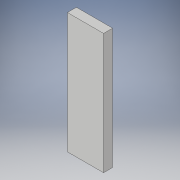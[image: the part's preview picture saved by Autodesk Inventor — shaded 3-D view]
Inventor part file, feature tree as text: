
AUTODESK INVENTOR PART (.ipt)
format: ipt  version: 2017 (Build 210142000, 142)  size: 97,792 bytes
history: native  units: in
note: dims shown in document units (in); Inventor stores cm internally (conversion verified against a paired STEP export)
features: extrude x1, sketch x1
ambient origin geometry x8: Origin, YZ Plane, XZ Plane, XY Plane, X Axis, Y Axis, Z Axis, Center Point
bodies: Solid1 (feature_tree)
feature tree (2):
  extrude  "door half"  Depth=6.6667in
  sketch  "Sketch1"  dims[d0=2.0in d1=6.6667in d3=0.5in d4=0.0in]
